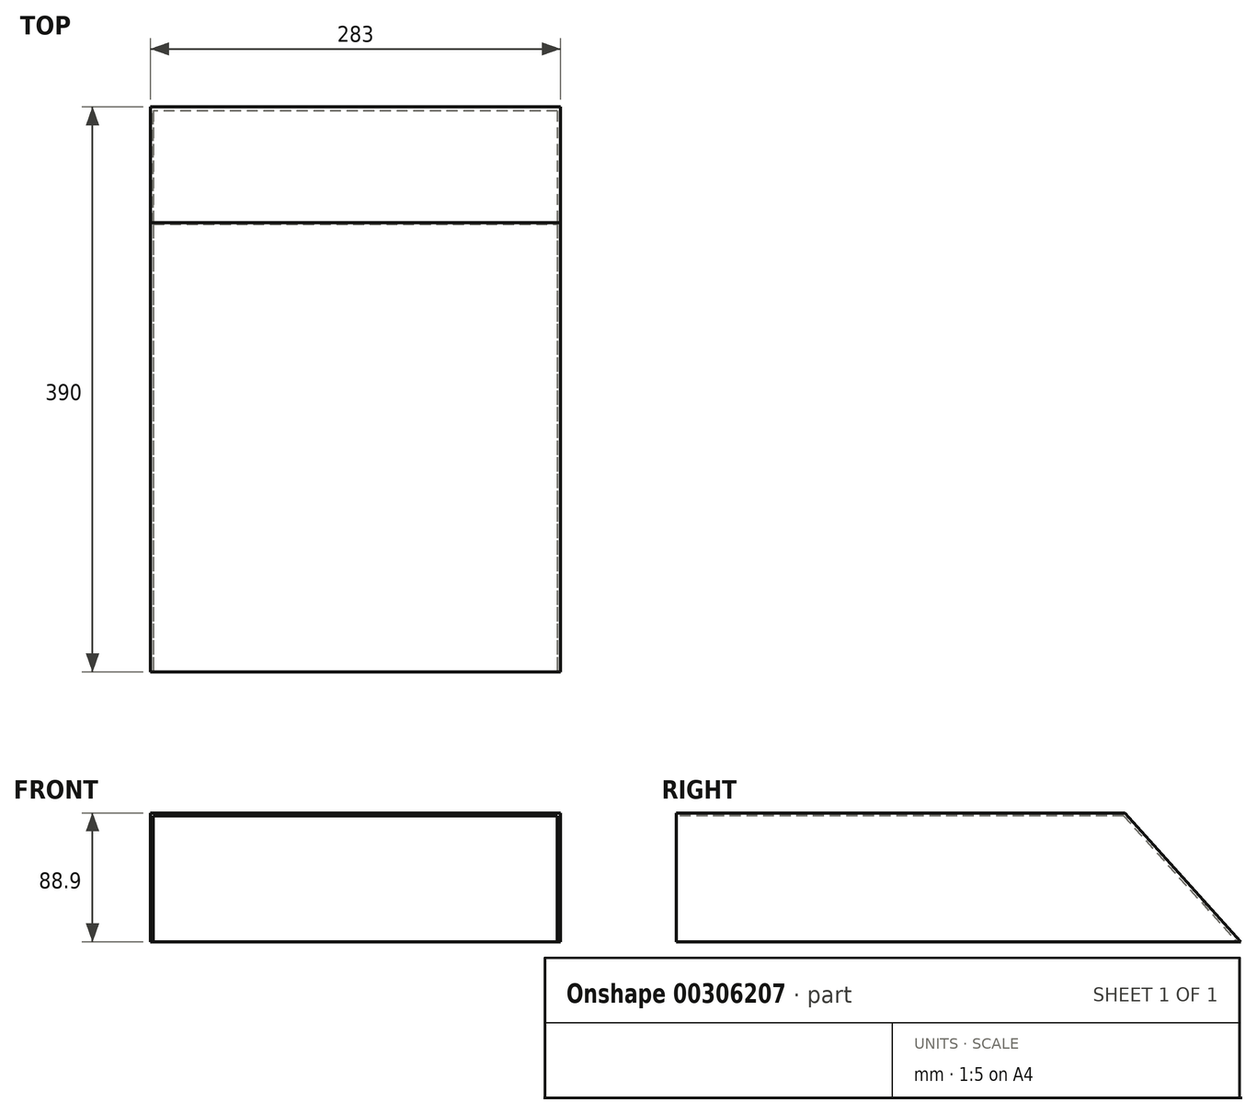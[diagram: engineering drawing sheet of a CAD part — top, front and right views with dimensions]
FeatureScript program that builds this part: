
annotation { "Feature Type Name" : "Feature", "Feature Type Description" : "" }
export const myFeature = defineFeature(function(context is Context, id is Id, definition is map)
    precondition{}
    {
        {
            var Q0;
            Q0=qCreatedBy(makeId("Top.planeOp"),FACE);
            var sketch = newSketch(context, id + "F0", { "sketchPlane" : qUnion([Q0])});
            skLineSegment(sketch, "E0.bottom", {"start": v(-141.5, 195) * mm, "end": v(141.5, 195) * mm});
            skLineSegment(sketch, "E0.top", {"start": v(-141.5, -195) * mm, "end": v(141.5, -195) * mm});
            skLineSegment(sketch, "E0.left", {"start": v(-141.5, 195) * mm, "end": v(-141.5, -195) * mm});
            skLineSegment(sketch, "E0.right", {"start": v(141.5, 195) * mm, "end": v(141.5, -195) * mm});
            skPoint(sketch, "E0.middle", {"position": v(0, 0) * mm});
            skSolve(sketch);
        }
        {
            var Q0;
            Q0=makeQuery(id+"F0.imprint","IMPRINT",FACE,{"disambiguationData":[TD([[makeQuery(id+"F0.imprint","IMPRINT",EDGE,{"derivedFrom":sQuery(id+"F0.wireOp",EDGE,"E0.bottom")}),-1.0]])]});
            extrude(context, id + "F1", {"entities" : qUnion([Q0]), "depth" : 88.9 * mm});
        }
        {
            var Q0;
            Q0=makeQuery(id+"F1.opExtrude","SWEPT_FACE",FACE,{"disambiguationData":[OSD([sQuery(id+"F0.wireOp",EDGE,"E0.left")])]});
            var sketch = newSketch(context, id + "F2", { "sketchPlane" : qUnion([Q0])});
            skLineSegment(sketch, "E1.0", {"start": v(-195, 88.9) * mm, "end": v(195, 88.9) * mm});
            skLineSegment(sketch, "E1.1", {"start": v(-195, 88.9) * mm, "end": v(-195, 0) * mm});
            skLineSegment(sketch, "E1.2", {"start": v(-195, 0) * mm, "end": v(195, 0) * mm});
            skLineSegment(sketch, "E2", {"start": v(-115, 88.9) * mm, "end": v(-195, 0) * mm});
            skLineSegment(sketch, "E3.0", {"start": v(-112.3, 88.9) * mm, "end": v(-192.3, 0) * mm});
            skSolve(sketch);
        }
        {
            var Q0;
            {var subQ0=sQuery(id+"F2.wireOp",EDGE,"E1.1");Q0=makeQuery(id+"F2.imprint","IMPRINT",FACE,{"disambiguationData":[TD([[makeQuery(id+"F2.imprint","IMPRINT",EDGE,{"derivedFrom":subQ0}),1.0]])]});}
            extrude(context, id + "F3", {"entities" : qUnion([Q0]), "operationType" : NewBodyOperationType.REMOVE, "endBound" : BoundingType.THROUGH_ALL, "oppositeDirection" : true, "depth" : 25 * mm});
        }
        {
            var Q0;
            Q0=makeQuery(id+"F1.opExtrude","SWEPT_FACE",FACE,{"disambiguationData":[OSD([sQuery(id+"F0.wireOp",EDGE,"E0.top")])]});
            var sketch = newSketch(context, id + "F4", { "sketchPlane" : qUnion([Q0])});
            skLineSegment(sketch, "E4.0", {"start": v(139.5, 86.9) * mm, "end": v(139.5, 0) * mm});
            skLineSegment(sketch, "E4.1", {"start": v(-139.5, 86.9) * mm, "end": v(139.5, 86.9) * mm});
            skLineSegment(sketch, "E4.2", {"start": v(-139.5, 86.9) * mm, "end": v(-139.5, 0) * mm});
            skSolve(sketch);
        }
        {
            var Q0;
            {var subQ0=sQuery(id+"F4.wireOp",EDGE,"E4.0");Q0=makeQuery(id+"F4.imprint","IMPRINT",FACE,{"disambiguationData":[TD([[makeQuery(id+"F4.imprint","IMPRINT",EDGE,{"derivedFrom":subQ0}),-1.0]])]});}
            extrude(context, id + "F5", {"entities" : qUnion([Q0]), "operationType" : NewBodyOperationType.REMOVE, "endBound" : BoundingType.THROUGH_ALL, "oppositeDirection" : true, "depth" : 25 * mm});
        }
        {
            var Q0;
            {var subQ0=sQuery(id+"F2.wireOp",EDGE,"E2");Q0=makeQuery(id+"F2.imprint","IMPRINT",FACE,{"disambiguationData":[TD([[makeQuery(id+"F2.imprint","IMPRINT",EDGE,{"derivedFrom":subQ0}),1.0]])]});}
            var Q1;
            Q1=makeQuery(id+"F5.boolean.opBoolean","COPY",FACE,{"derivedFrom":makeQuery(id+"F5.opExtrude","SWEPT_FACE",FACE,{"disambiguationData":[OSD([sQuery(id+"F4.wireOp",EDGE,"E4.0")])]})});
            extrude(context, id + "F6", {"entities" : qUnion([Q0]), "operationType" : NewBodyOperationType.ADD, "endBound" : BoundingType.UP_TO_SURFACE, "oppositeDirection" : true, "endBoundEntityFace" : qUnion([Q1]), "depth" : 25 * mm});
        }
    });
